# Revit family: SoapLiquidDispenser-ContactlessLiquidSoapDispenser-Short-ElectricallyConnected-Vitra-OriginSeries-A44699
name_source: partatom
category: Plumbing Fixtures
revit_build: Autodesk Revit 2017 (Build: 20160225_1515(x64)
units: mm (PartAtom-declared; Revit-internal decimal feet)

## family parameters
Cut with Voids When Loaded = No
Host = Face
OmniClass Number = 23.45.00.00
OmniClass Title = Sanitary, Laundry, and Cleaning Equipment
Part Type = Normal
Room Calculation Point = No
Round Connector Dimension = Use Diameter
Shared = Yes

## types (4) — shared parameters
BIMobject category = Sanitary - Dispensers
Brand = VitrA
CW Connection = No
Description = Origin Liquid Soap Dispenser - Contactless Liquid Soap Dispenser - Short - Electrically Connected
Design country = Turkey
HW Connection = No
IFC Classification = Sanitary Terminal
Main Material = Metal
Manufacturer = Vitra
Manufacturer name = Vitra
Masterformat 2014 Code = 12 00 00
Masterformat 2014 Description = Furnishings
NBS Referans Code = 35-76-80
NBS Referans Description = Soap Dispensers
Nominal Depth (mm) = 145 mm  [stored 0.475722 ft]
Nominal Height (mm) = 105 mm  [stored 0.344488 ft]
Nominal Width (mm) = 60 mm  [stored 0.19685 ft]
OmniClass Code = 23-31 25 29 13
OmniClass Description = Hand Soap Dispensers
Product Properties = Liquid Soap Dispenser
Product Type = Liquid Soap Dispenser
Product certification = https://www.vitraglobal.com
Product family = OriginSeries
Product group = Liquid Soap Dispenser
Product url = https://www.vitraglobal.com
Technical description = https://www.vitraglobal.com
UNSPSC Description = Sanitary ware
URL = https://vitraglobal.com
Uniclass 1.4 Code = L8246
Uniclass 1.4 Description = Soap holders/dispensers
Uniclass 2.0 Code = PR-35-76-80
Uniclass 2.0 Description = Soap Dispensers
Uniclass 2015 Code = Pr_40_70_22_81
Uniclass 2015 Name = Soap dispensers
Uniformat II Code = E20
Uniformat II Description = FURNISHINGS
Vent Connection = No
Warranty Period (Year) = 5 years
Waste Connection = No
Weight Net (kg) = 0.85
Youtube = https://www.youtube.com
zero-valued in all types: Default Elevation

## per-type parameters (varying)
| type | Article No. (default) | Coating Material | Color | Model | Product SKU | Product data url |
| SoapLiquidDispenser-ContactlessLiquidSoapDispenser-Short-ElectricallyConnected-Vitra-OriginSeries-A44699 | A44699 | Chrome | Chrome | A44699 | A44699 | https://www.bimobject.com |
| SoapLiquidDispenser-ContactlessLiquidSoapDispenser-Short-ElectricallyConnected-Vitra-OriginSeries-A4469926 | A4469926 | Copper | Copper | A4469926 | A4469926 |  |
| SoapLiquidDispenser-ContactlessLiquidSoapDispenser-Short-ElectricallyConnected-Vitra-OriginSeries-A4469934 | A4469934 | Brushed Nickel | Brushed Nickel | A4469934 | A4469934 |  |
| SoapLiquidDispenser-ContactlessLiquidSoapDispenser-Short-ElectricallyConnected-Vitra-OriginSeries-A4469936 | A4469936 | Black | Matte Black | A4469936 | A4469936 |  |

note: [stored X ft] marks values corroborated as IEEE doubles in the binary element streams (Revit-internal decimal feet)

## geometry (parser evidence)
native form markers: Sweep x3
no freeform markers — native parametric forms only
